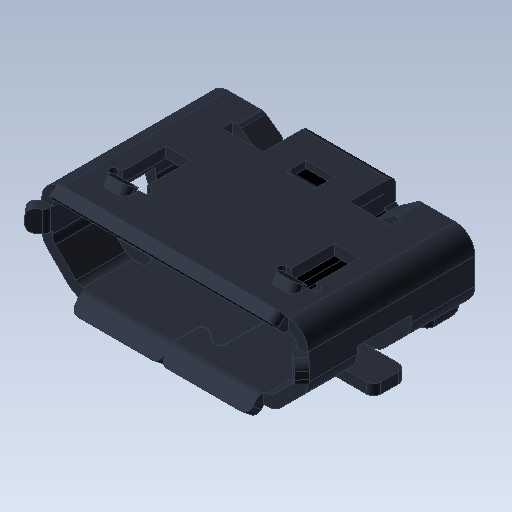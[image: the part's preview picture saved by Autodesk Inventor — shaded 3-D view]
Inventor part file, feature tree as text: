
AUTODESK INVENTOR PART (.ipt)
format: ipt  version: 2020 (Build 240168000, 168)  size: 460,288 bytes
history: native  units: in
note: dims shown in document units (in); Inventor stores cm internally (conversion verified against a paired STEP export)
features: fillet x1
ambient origin geometry x8: Origin, YZ Plane, XZ Plane, XY Plane, X Axis, Y Axis, Z Axis, Center Point
bodies: Solid1 (feature_tree)
feature tree (1):
  fillet  "Fillet13"  [1 undecoded]
note: 1 required parameter value undecoded (feature->parameter linkage not recoverable at this tier; creation-order binding heuristic only, values carry confidence <= 0.55)
